# Revit family: РОСМА_ДатчикДавл_РПД
name_source: partatom
category: Арматура трубопроводов
revit_build: Autodesk Revit 2018 (Build: 20180423_1000(x64)
units: mm (PartAtom-declared; Revit-internal decimal feet)

## family parameters
Всегда вертикально = Да
На основе рабочей плоскости = Нет
Общий = Нет
При загрузке вырезать с полостями = Нет
Размер круглого соединителя = Использовать диаметр
Тип детали = Вставляется

## types (1)
- РПД
    A = 36 мм
    ADSK_Версия Revit = v2018
    ADSK_Версия семейства = 1.0
    ADSK_Единица измерения = шт.
    ADSK_Количество = 1
    C = 93 мм
    DN = 15 мм
    L = 16 мм
    S = 22 мм
    S1 = 13 мм
    Table = спец_РПД
    URL = https://rosma.spb.ru
    h = 69 мм
    Группа модели = Оборудование
    Давление01 = ‎ : РПД-В -0.1…0МПа
    Давление02 = ‎ : РПД-И 0…0.1МПа
    Давление03 = ‎ : РПД-И 0…0.16МПа
    Давление04 = ‎ : РПД-И 0…0.25МПа
    Давление05 = ‎ : РПД-И 0…0.4МПа
    Давление06 = ‎ : РПД-И 0…0.6МПа
    Давление07 = ‎ : РПД-И 0…1.0МПа
    Давление08 = ‎ : РПД-И 0…1.6МПа
    Давление09 = ‎ : РПД-И 0…2.5МПа
    Давление10 = ‎ : РПД-И 0…4МПа
    Давление11 = ‎ : РПД-И 0…6МПа
    Давление12 = ‎ : РПД-И 0…10МПа
    Давление13 = ‎ : РПД-И 0…16МПа
    Давление14 = ‎ : РПД-И 0…25МПа
    Давление15 = ‎ : РПД-И 0…40МПа
    Давление16 = ‎ : РПД-И 0…60МПа
    Давление17 = ‎ : РПД-И 0…100МПа
    Давление18 = ‎ : РПД-ИВ -0.1…0.1МПа
    Давление19 = ‎ : РПД-ИВ -0.1…0.3МПа
    Давление20 = ‎ : РПД-ИВ -0.1…0.5МПа
    Давление21 = ‎ : РПД-ИВ -0.1…0.9МПа
    Давление22 = ‎ : РПД-ИВ -0.1…1.5МПа
    Давление23 = ‎ : РПД-ИВ -0.1…2.4МПа
    Изготовитель = ЗАО "РОСМА"
    Материал корпуса 1 = _Белый металлик
    Материал корпуса 2 = _Черный пластик
    Межповерочный интервал = 5 лет
    Описание = Датчики давления РПД-И (РПД-В, РПД-ИВ) предназначены для измерения и непрерывного преобразования избыточного (РПД-И), вакуумметрического (РПД-В), вакуумметрического и избыточного (РПД-ИВ) давлений в унифицированный выходной сигнал постоянного тока. Измеряемые среды — не кристаллизующиеся жидкости, газы и пары, неагрессивные к нержавеющей стали. 
Область применения: системы сбора данных, автоматического контроля, регулирования и управления технологическими процессами в различных отраслях промышленности и городского хозяйства.
    Техническая документация = НСРП.421262.001ТУ; ГОСТ 22520–85
